# Revit family: CONV_Zero_GnrlPrpseLmnrs_MistPendant
name_source: partatom
category: Lighting Fixtures
revit_build: Autodesk Revit 2015 (Build: 20140606_1530(x64)
units: mm (PartAtom-declared; Revit-internal decimal feet)

## types (18) — shared parameters
AssetType = Fixed
BIMObjectName = CONV_Zero_GnrlPrpseLmnrs_MistPendant
Brand = Zero
Category = Pendant
Collection = Mist
Color Filter = 16777215
Designer = Front Design 2017
Dimming Lamp Color Temperature Shift = <None>
DurationUnit = Year
Emit Shape Visible in Rendering = No
ExpiringDate = 07/2018
Features = Terminal block inside canopy
Finish = White painted metal, matt acrylic
HasProtectiveEarth = Yes
IP_Code = IP20
IfcExportAs = IfcLightFixtureType
IfcExportType = NOTDEFINED
LensMaterial = Difused glass
LightFixtureMountingType = Suspended
LightFixturePlacingType = Ceiling
Manufacturer = Zero
ManufacturerName = Zero
ManufacturerURL = https://www.zerolighting.com
Material = Metal and acrylic
NBSDescription = General purpose luminaires
NBSReference = 90-60-50/405
Name = GnrlPrpseLmnrs_MistPendant
NominalCurrent = 0 A
NominalFrequencyRange = 50 Hz
NominalVoltage = 230 V
NominalVoltageCalc = 0 V
NumberOfPoles = 1
PhaseAngle = 0.00°
Shape = Sculptured
Tilt Angle = 90.00°
URL = https://www.zerolighting.com
Uniclass2 = Pr_70_70_49_86
Uniclass2015Description = Suspended luminaires
Uniclass2015Reference = Pr_70_70_48_86
UsageCurrent = 0 A
Version = 1
VersionDate = 13/01/2018
WarrantyDurationUnit = Year
zero-valued in all types: DefaultElevation, ElectricalDeviceNominalPower, MaintenanceFactor, NumberOfSources

## per-type parameters (varying)
| type | ArticleNumber | Color | ConvergoRefNr | Dimming | Emit from Circle Diameter | LightFixtureMainMaterial | ModelNumber | ModelType | NominalDiameter | NominalHeight | NominalLength | NominalRadius | NominalWidth | Photometric Web File | Size | TotalWattage |
| Mist pendant 250 LED 880LM/9W Opal | 8365-1-01 | Opal | 0046-1708-0033-SE |  | 250 mm  [stored 0.82021 ft] | Opalwhite | 8365-1-01 | mist-pendel-250 | 250 mm  [stored 0.82021 ft] | 137 mm  [stored 0.449475 ft] | 250 mm  [stored 0.82021 ft] | 125 mm  [stored 0.410105 ft] | 250 mm  [stored 0.82021 ft] | Mist83651.IES | 250x250x137 mm | 9 W |
| Mist pendant 350 LED 1947LM/26W Opal | 8365-3-01 | Opal | 0046-1708-0034-SE |  | 350 mm  [stored 1.14829 ft] | Opalwhite | 8365-3-01 | mist-pendel-350 | 350 mm  [stored 1.14829 ft] | 193 mm  [stored 0.633202 ft] | 350 mm  [stored 1.14829 ft] | 175 mm  [stored 0.574147 ft] | 350 mm  [stored 1.14829 ft] | Mist83653.IES | 350x350x193 mm | 26 W |
| Mist pendant 450 LED 2130LM/26W Opal | 8365-5-01 | Opal | 0046-1708-0035-SE |  | 450 mm  [stored 1.47638 ft] | Opalwhite | 8365-5-01 | mist-pendel-450 | 450 mm  [stored 1.47638 ft] | 247 mm | 450 mm  [stored 1.47638 ft] | 225 mm  [stored 0.738189 ft] | 450 mm  [stored 1.47638 ft] | Mist83655.IES | 450x450x247 mm | 26 W |
| Mist pendant 250 LED 880LM/9W Yellow | 8365-1-14 | Yellow | 0046-1708-0033-SE |  | 250 mm  [stored 0.82021 ft] | Yellow | 8365-1-14 | mist-pendel-250 | 250 mm  [stored 0.82021 ft] | 137 mm  [stored 0.449475 ft] | 250 mm  [stored 0.82021 ft] | 125 mm  [stored 0.410105 ft] | 250 mm  [stored 0.82021 ft] | Mist83651.IES | 250x250x137 mm | 9 W |
| Mist pendant 250 LED 880LM/9W Pink | 8365-1-42 | Pink | 0046-1708-0033-SE |  | 250 mm  [stored 0.82021 ft] | Pink | 8365-1-42 | mist-pendel-250 | 250 mm  [stored 0.82021 ft] | 137 mm  [stored 0.449475 ft] | 250 mm  [stored 0.82021 ft] | 125 mm  [stored 0.410105 ft] | 250 mm  [stored 0.82021 ft] | Mist83651.IES | 250x250x137 mm | 9 W |
| Mist pendant 350 LED 1947LM/26W Yellow | 8365-3-14 | Yellow | 0046-1708-0034-SE |  | 350 mm  [stored 1.14829 ft] | Yellow | 8365-3-14 | mist-pendel-350 | 350 mm  [stored 1.14829 ft] | 193 mm  [stored 0.633202 ft] | 350 mm  [stored 1.14829 ft] | 175 mm  [stored 0.574147 ft] | 350 mm  [stored 1.14829 ft] | Mist83653.IES | 350x350x193 mm | 26 W |
| Mist pendant 350 LED 1947LM/26W Pink | 8365-3-42 | Pink | 0046-1708-0034-SE |  | 350 mm  [stored 1.14829 ft] | Pink | 8365-3-42 | mist-pendel-350 | 350 mm  [stored 1.14829 ft] | 193 mm  [stored 0.633202 ft] | 350 mm  [stored 1.14829 ft] | 175 mm  [stored 0.574147 ft] | 350 mm  [stored 1.14829 ft] | Mist83653.IES | 350x350x193 mm | 26 W |
| Mist pendant 450 LED 2130LM/26W Yellow | 8365-5-14 | Yellow | 0046-1708-0035-SE |  | 450 mm  [stored 1.47638 ft] | Yellow | 8365-5-14 | mist-pendel-450 | 450 mm  [stored 1.47638 ft] | 247 mm | 450 mm  [stored 1.47638 ft] | 225 mm  [stored 0.738189 ft] | 450 mm  [stored 1.47638 ft] | Mist83655.IES | 450x450x247 mm | 26 W |
| Mist pendant 450 LED 2130LM/26W Pink | 8365-5-42 | Pink | 0046-1708-0035-SE |  | 450 mm  [stored 1.47638 ft] | Pink | 8365-5-42 | mist-pendel-450 | 450 mm  [stored 1.47638 ft] | 247 mm | 450 mm  [stored 1.47638 ft] | 225 mm  [stored 0.738189 ft] | 450 mm  [stored 1.47638 ft] | Mist83655.IES | 450x450x247 mm | 26 W |
| Mist pendant 250 LED 880LM/9W Opal HFF | 8365-1-01HFF | Opal | 0046-1708-0033-SE | Dimmable DALI or SwitchDim | 250 mm  [stored 0.82021 ft] | Opalwhite | 8365-1-01HFF | mist-pendel-250 | 250 mm  [stored 0.82021 ft] | 137 mm  [stored 0.449475 ft] | 250 mm  [stored 0.82021 ft] | 125 mm  [stored 0.410105 ft] | 250 mm  [stored 0.82021 ft] | Mist83651.IES | 250x250x137 mm | 9 W |
| Mist pendant 250 LED 880LM/9W Pink HFF | 8365-1-42HFF | Pink | 0046-1708-0033-SE | Dimmable DALI or SwitchDim | 250 mm  [stored 0.82021 ft] | Pink | 8365-1-42HFF | mist-pendel-250 | 250 mm  [stored 0.82021 ft] | 137 mm  [stored 0.449475 ft] | 250 mm  [stored 0.82021 ft] | 125 mm  [stored 0.410105 ft] | 250 mm  [stored 0.82021 ft] | Mist83651.IES | 250x250x137 mm | 9 W |
| Mist pendant 250 LED 880LM/9W Yellow HFF | 8365-1-14HFF | Yellow | 0046-1708-0033-SE | Dimmable DALI or SwitchDim | 250 mm  [stored 0.82021 ft] | Yellow | 8365-1-14HFF | mist-pendel-250 | 250 mm  [stored 0.82021 ft] | 137 mm  [stored 0.449475 ft] | 250 mm  [stored 0.82021 ft] | 125 mm  [stored 0.410105 ft] | 250 mm  [stored 0.82021 ft] | Mist83651.IES | 250x250x137 mm | 9 W |
| Mist pendant 350 LED 1947LM/26W Opal HFF | 8365-3-01HFF | Opal | 0046-1708-0034-SE | Dimmable DALI or SwitchDim | 350 mm  [stored 1.14829 ft] | Opalwhite | 8365-3-01HFF | mist-pendel-350 | 350 mm  [stored 1.14829 ft] | 193 mm  [stored 0.633202 ft] | 350 mm  [stored 1.14829 ft] | 175 mm  [stored 0.574147 ft] | 350 mm  [stored 1.14829 ft] | Mist83653.IES | 350x350x193 mm | 26 W |
| Mist pendant 350 LED 1947LM/26W Pink HFF | 8365-3-42HFF | Pink | 0046-1708-0034-SE | Dimmable DALI or SwitchDim | 350 mm  [stored 1.14829 ft] | Pink | 8365-3-42HFF | mist-pendel-350 | 350 mm  [stored 1.14829 ft] | 193 mm  [stored 0.633202 ft] | 350 mm  [stored 1.14829 ft] | 175 mm  [stored 0.574147 ft] | 350 mm  [stored 1.14829 ft] | Mist83653.IES | 350x350x193 mm | 26 W |
| Mist pendant 350 LED 1947LM/26W Yellow HFF | 8365-3-14HFF | Yellow | 0046-1708-0034-SE | Dimmable DALI or SwitchDim | 350 mm  [stored 1.14829 ft] | Yellow | 8365-3-14HFF | mist-pendel-350 | 350 mm  [stored 1.14829 ft] | 193 mm  [stored 0.633202 ft] | 350 mm  [stored 1.14829 ft] | 175 mm  [stored 0.574147 ft] | 350 mm  [stored 1.14829 ft] | Mist83653.IES | 350x350x193 mm | 26 W |
| Mist pendant 450 LED 2130LM/26W Opal HFF | 8365-5-01HFF | Opal | 0046-1708-0035-SE | Dimmable DALI or SwitchDim | 450 mm  [stored 1.47638 ft] | Opalwhite | 8365-5-01HFF | mist-pendel-450 | 450 mm  [stored 1.47638 ft] | 247 mm | 450 mm  [stored 1.47638 ft] | 225 mm  [stored 0.738189 ft] | 450 mm  [stored 1.47638 ft] | Mist83655.IES | 450x450x247 mm | 26 W |
| Mist pendant 450 LED 2130LM/26W Pink HFF | 8365-5-42HFF | Pink | 0046-1708-0035-SE | Dimmable DALI or SwitchDim | 450 mm  [stored 1.47638 ft] | Pink | 8365-5-42HFF | mist-pendel-450 | 450 mm  [stored 1.47638 ft] | 247 mm | 450 mm  [stored 1.47638 ft] | 225 mm  [stored 0.738189 ft] | 450 mm  [stored 1.47638 ft] | Mist83655.IES | 450x450x247 mm | 26 W |
| Mist pendant 450 LED 2130LM/26W Yellow HFF | 8365-5-14HFF | Yellow | 0046-1708-0035-SE | Dimmable DALI or SwitchDim | 450 mm  [stored 1.47638 ft] | Yellow | 8365-5-14HFF | mist-pendel-450 | 450 mm  [stored 1.47638 ft] | 247 mm | 450 mm  [stored 1.47638 ft] | 225 mm  [stored 0.738189 ft] | 450 mm  [stored 1.47638 ft] | Mist83655.IES | 450x450x247 mm | 26 W |

note: column(s) folded — value = type name in every type: Model

note: [stored X ft] marks values corroborated as IEEE doubles in the binary element streams (Revit-internal decimal feet)

## geometry (parser evidence)
native form markers: Sweep x12
no freeform markers — native parametric forms only
